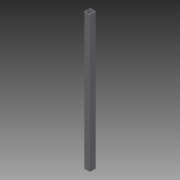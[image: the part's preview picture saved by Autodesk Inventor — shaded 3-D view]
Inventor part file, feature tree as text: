
AUTODESK INVENTOR PART (.ipt)
format: ipt  version: 2013 (Build 170138000, 138)  size: 86,016 bytes
history: native  units: in
note: dims shown in document units (in); Inventor stores cm internally (conversion verified against a paired STEP export)
features: extrude x2, sketch x2
ambient origin geometry x8: Origin, YZ Plane, XZ Plane, XY Plane, X Axis, Y Axis, Z Axis, Center Point
bodies: Solid1 (feature_tree)
feature tree (4):
  extrude  "Extrusion1"  Depth=1.0in
  extrude  "Extrusion2"  Depth=36.0in TaperAngle=0.0deg
  sketch  "Sketch1"  dims[d0=1.0in d2=1.0in]
  sketch  "Sketch2"  dims[d3=0.0625in d4=36.0in d5=0.0in d6=23.5in d7=23.5213in d8=36.0in d9=0.0in]
